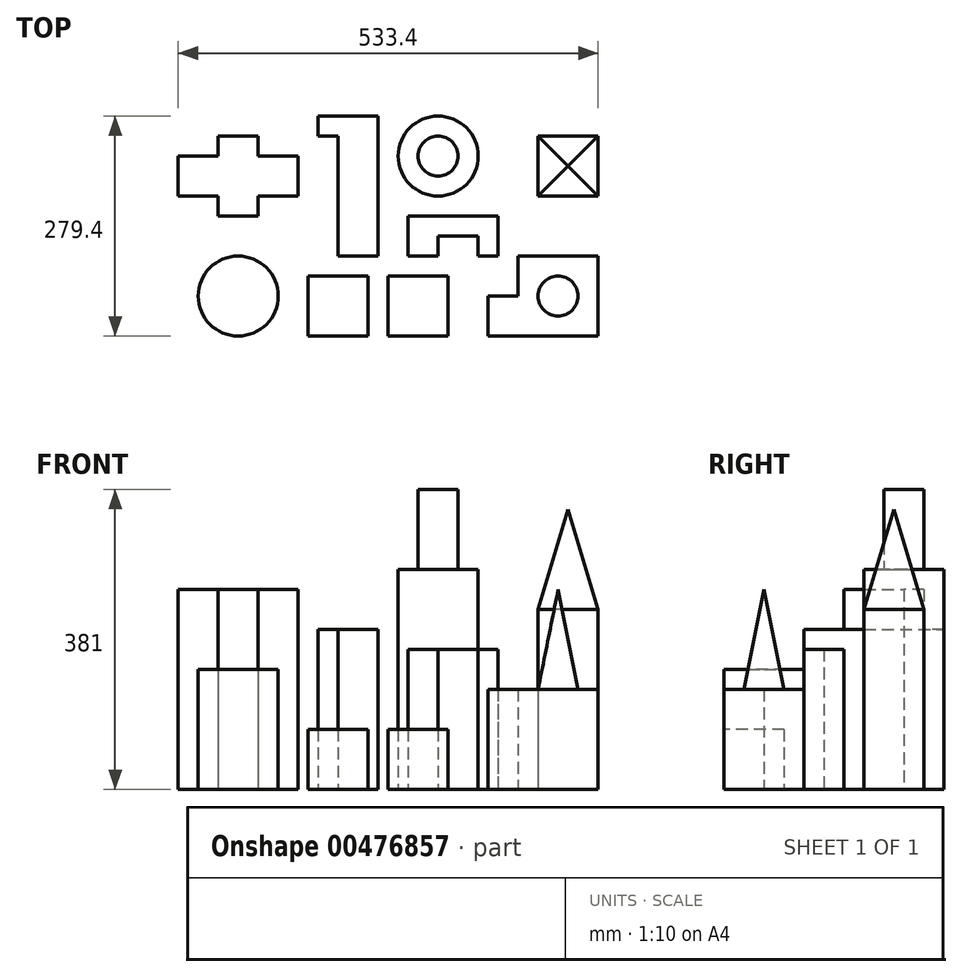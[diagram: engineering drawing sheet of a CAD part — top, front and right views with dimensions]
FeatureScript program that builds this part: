
annotation { "Feature Type Name" : "Feature", "Feature Type Description" : "" }
export const myFeature = defineFeature(function(context is Context, id is Id, definition is map)
    precondition{}
    {
        {
            var Q0;
            Q0=qCreatedBy(makeId("Top.planeOp"),FACE);
            var sketch = newSketch(context, id + "F0", { "sketchPlane" : qUnion([Q0])});
            skLineSegment(sketch, "E0", {"start": v(130.25, 0) * mm, "end": v(130.25, -50.8) * mm});
            skLineSegment(sketch, "E1", {"start": v(130.25, -50.8) * mm, "end": v(269.95, -50.8) * mm});
            skLineSegment(sketch, "E2", {"start": v(269.95, -50.8) * mm, "end": v(269.95, 50.8) * mm});
            skLineSegment(sketch, "E3", {"start": v(269.95, 50.8) * mm, "end": v(168.35, 50.8) * mm});
            skLineSegment(sketch, "E4", {"start": v(168.35, 50.8) * mm, "end": v(168.35, 0) * mm});
            skLineSegment(sketch, "E5", {"start": v(168.35, 0) * mm, "end": v(130.25, 0) * mm});
            skSolve(sketch);
        }
        {
            var Q0;
            Q0 = qSketchRegion(id + "F0", true);
            extrude(context, id + "F1", {"entities" : qUnion([Q0]), "depth" : 127 * mm});
        }
        {
            var Q0;
            Q0=makeQuery(id+"F1.opExtrude","CAP_FACE",FACE,{"disambiguationData":[OSD([sQuery(id+"F0.wireOp",EDGE,"E0"),sQuery(id+"F0.wireOp",EDGE,"E1"),sQuery(id+"F0.wireOp",EDGE,"E2"),sQuery(id+"F0.wireOp",EDGE,"E3"),sQuery(id+"F0.wireOp",EDGE,"E4"),sQuery(id+"F0.wireOp",EDGE,"E5")])],"isStart":false});
            var sketch = newSketch(context, id + "F2", { "sketchPlane" : qUnion([Q0])});
            skCircle(sketch, "E6", {"center": v(219.15, 0) * mm, "radius": 25.4 * mm});
            skSolve(sketch);
        }
        {
            var Q0;
            Q0=makeQuery(id+"F2.imprint","IMPRINT",FACE,{"disambiguationData":[TD([[makeQuery(id+"F2.imprint","IMPRINT",EDGE,{"derivedFrom":sQuery(id+"F2.wireOp",EDGE,"E6")}),1.0]])]});
            extrude(context, id + "F3", {"entities" : qUnion([Q0]), "operationType" : NewBodyOperationType.ADD, "depth" : 127 * mm});
        }
        {
            var Q0;
            Q0=makeQuery(id+"F3.opExtrude","CAP_FACE",FACE,{"disambiguationData":[OSD([sQuery(id+"F2.wireOp",EDGE,"E6")])],"isStart":false});
            chamfer(context, id + "F4", {"entities" : qUnion([Q0]), "chamferType" : ChamferType.TWO_OFFSETS, "width1" : 25.4 * mm, "oppositeDirection" : false, "width2" : 127 * mm, "tangentPropagation" : true});
        }
        {
            var Q0;
            Q0=qCreatedBy(makeId("Top.planeOp"),FACE);
            var sketch = newSketch(context, id + "F5", { "sketchPlane" : qUnion([Q0])});
            skLineSegment(sketch, "E7.bottom", {"start": v(3.25, 25.4) * mm, "end": v(79.45, 25.4) * mm});
            skLineSegment(sketch, "E7.top", {"start": v(3.25, -50.8) * mm, "end": v(79.45, -50.8) * mm});
            skLineSegment(sketch, "E7.left", {"start": v(3.25, 25.4) * mm, "end": v(3.25, -50.8) * mm});
            skLineSegment(sketch, "E7.right", {"start": v(79.45, 25.4) * mm, "end": v(79.45, -50.8) * mm});
            skLineSegment(sketch, "E8.bottom", {"start": v(-98.35, 25.4) * mm, "end": v(-22.15, 25.4) * mm});
            skLineSegment(sketch, "E8.top", {"start": v(-98.35, -50.8) * mm, "end": v(-22.15, -50.8) * mm});
            skLineSegment(sketch, "E8.left", {"start": v(-98.35, 25.4) * mm, "end": v(-98.35, -50.8) * mm});
            skLineSegment(sketch, "E8.right", {"start": v(-22.15, 25.4) * mm, "end": v(-22.15, -50.8) * mm});
            skSolve(sketch);
        }
        {
            var Q0;
            Q0 = qSketchRegion(id + "F5", true);
            extrude(context, id + "F6", {"bodyType" : ToolBodyType.SURFACE, "surfaceEntities" : qUnion([Q0]), "depth" : 76.2 * mm});
        }
        {
            var Q0;
            Q0=qCreatedBy(makeId("Top.planeOp"),FACE);
            var sketch = newSketch(context, id + "F7", { "sketchPlane" : qUnion([Q0])});
            skCircle(sketch, "E9", {"center": v(-187.25, 0) * mm, "radius": 50.8 * mm});
            skSolve(sketch);
        }
        {
            var Q0;
            Q0=makeQuery(id+"F7.imprint","IMPRINT",FACE,{"disambiguationData":[TD([[makeQuery(id+"F7.imprint","IMPRINT",EDGE,{"derivedFrom":sQuery(id+"F7.wireOp",EDGE,"E9")}),1.0]])]});
            var Q1;
            Q1=sQuery(id+"F7.wireOp",EDGE,"E9");
            extrude(context, id + "F8", {"entities" : qUnion([Q0]), "surfaceEntities" : qUnion([Q1]), "depth" : 152.4 * mm});
        }
        {
            var Q0;
            Q0=qCreatedBy(makeId("Top.planeOp"),FACE);
            var sketch = newSketch(context, id + "F9", { "sketchPlane" : qUnion([Q0])});
            skLineSegment(sketch, "E10", {"start": v(-263.45, 177.8) * mm, "end": v(-212.65, 177.8) * mm});
            skLineSegment(sketch, "E11", {"start": v(-212.65, 177.8) * mm, "end": v(-212.65, 203.2) * mm});
            skLineSegment(sketch, "E12", {"start": v(-212.65, 203.2) * mm, "end": v(-161.85, 203.2) * mm});
            skLineSegment(sketch, "E13", {"start": v(-161.85, 203.2) * mm, "end": v(-161.85, 177.8) * mm});
            skLineSegment(sketch, "E14", {"start": v(-161.85, 177.8) * mm, "end": v(-111.05, 177.8) * mm});
            skLineSegment(sketch, "E15", {"start": v(-111.05, 177.8) * mm, "end": v(-111.05, 127) * mm});
            skLineSegment(sketch, "E16", {"start": v(-111.05, 127) * mm, "end": v(-161.85, 127) * mm});
            skLineSegment(sketch, "E17", {"start": v(-161.85, 127) * mm, "end": v(-161.85, 101.6) * mm});
            skLineSegment(sketch, "E18", {"start": v(-161.85, 101.6) * mm, "end": v(-212.65, 101.6) * mm});
            skLineSegment(sketch, "E19", {"start": v(-212.65, 101.6) * mm, "end": v(-212.65, 127) * mm});
            skLineSegment(sketch, "E20", {"start": v(-212.65, 127) * mm, "end": v(-263.45, 127) * mm});
            skLineSegment(sketch, "E21", {"start": v(-263.45, 127) * mm, "end": v(-263.45, 177.8) * mm});
            skSolve(sketch);
        }
        {
            var Q0;
            Q0 = qSketchRegion(id + "F9", true);
            extrude(context, id + "F10", {"entities" : qUnion([Q0]), "depth" : 254 * mm});
        }
        {
            var Q0;
            Q0=qCreatedBy(makeId("Top.planeOp"),FACE);
            var sketch = newSketch(context, id + "F11", { "sketchPlane" : qUnion([Q0])});
            skLineSegment(sketch, "E22", {"start": v(-60.25, 50.8) * mm, "end": v(-9.45, 50.8) * mm});
            skLineSegment(sketch, "E23", {"start": v(-9.45, 50.8) * mm, "end": v(-9.45, 228.6) * mm});
            skLineSegment(sketch, "E24", {"start": v(-9.45, 228.6) * mm, "end": v(-85.65, 228.6) * mm});
            skLineSegment(sketch, "E25", {"start": v(-85.65, 228.6) * mm, "end": v(-85.65, 203.2) * mm});
            skLineSegment(sketch, "E26", {"start": v(-85.65, 203.2) * mm, "end": v(-60.25, 203.2) * mm});
            skLineSegment(sketch, "E27", {"start": v(-60.25, 203.2) * mm, "end": v(-60.25, 50.8) * mm});
            skSolve(sketch);
        }
        {
            var Q0;
            Q0 = qSketchRegion(id + "F11", true);
            extrude(context, id + "F12", {"entities" : qUnion([Q0]), "depth" : 203.2 * mm});
        }
        {
            var Q0;
            Q0=qCreatedBy(makeId("Top.planeOp"),FACE);
            var sketch = newSketch(context, id + "F13", { "sketchPlane" : qUnion([Q0])});
            skCircle(sketch, "E28", {"center": v(66.75, 177.8) * mm, "radius": 50.8 * mm});
            skSolve(sketch);
        }
        {
            var Q0;
            Q0 = qSketchRegion(id + "F13", true);
            extrude(context, id + "F14", {"entities" : qUnion([Q0]), "depth" : 279.4 * mm});
        }
        {
            var Q0;
            Q0=makeQuery(id+"F14.opExtrude","CAP_FACE",FACE,{"disambiguationData":[OSD([sQuery(id+"F13.wireOp",EDGE,"E28")])],"isStart":false});
            var sketch = newSketch(context, id + "F15", { "sketchPlane" : qUnion([Q0])});
            skCircle(sketch, "E29", {"center": v(66.75, 177.8) * mm, "radius": 25.4 * mm});
            skSolve(sketch);
        }
        {
            var Q0;
            Q0=makeQuery(id+"F15.imprint","IMPRINT",FACE,{"disambiguationData":[TD([[makeQuery(id+"F15.imprint","IMPRINT",EDGE,{"derivedFrom":sQuery(id+"F15.wireOp",EDGE,"E29")}),1.0]])]});
            var Q1;
            Q1=sQuery(id+"F15.wireOp",EDGE,"E29");
            extrude(context, id + "F16", {"entities" : qUnion([Q0]), "operationType" : NewBodyOperationType.ADD, "surfaceEntities" : qUnion([Q1]), "depth" : 101.6 * mm});
        }
        {
            var Q0;
            Q0=qCreatedBy(makeId("Top.planeOp"),FACE);
            var sketch = newSketch(context, id + "F17", { "sketchPlane" : qUnion([Q0])});
            skLineSegment(sketch, "E30", {"start": v(28.65, 101.6) * mm, "end": v(28.65, 50.8) * mm});
            skLineSegment(sketch, "E31", {"start": v(28.65, 50.8) * mm, "end": v(66.75, 50.8) * mm});
            skLineSegment(sketch, "E32", {"start": v(66.75, 50.8) * mm, "end": v(66.75, 76.2) * mm});
            skLineSegment(sketch, "E33", {"start": v(66.75, 76.2) * mm, "end": v(117.55, 76.2) * mm});
            skLineSegment(sketch, "E34", {"start": v(117.55, 76.2) * mm, "end": v(117.55, 50.8) * mm});
            skLineSegment(sketch, "E35", {"start": v(117.55, 50.8) * mm, "end": v(142.95, 50.8) * mm});
            skLineSegment(sketch, "E36", {"start": v(142.95, 50.8) * mm, "end": v(142.95, 101.6) * mm});
            skLineSegment(sketch, "E37", {"start": v(142.95, 101.6) * mm, "end": v(28.65, 101.6) * mm});
            skSolve(sketch);
        }
        {
            var Q0;
            Q0 = qSketchRegion(id + "F17", true);
            extrude(context, id + "F18", {"entities" : qUnion([Q0]), "depth" : 177.8 * mm});
        }
        {
            var Q0;
            Q0=qCreatedBy(makeId("Top.planeOp"),FACE);
            var sketch = newSketch(context, id + "F19", { "sketchPlane" : qUnion([Q0])});
            skLineSegment(sketch, "E38.bottom", {"start": v(269.95, 203.2) * mm, "end": v(193.75, 203.2) * mm});
            skLineSegment(sketch, "E38.top", {"start": v(269.95, 127) * mm, "end": v(193.75, 127) * mm});
            skLineSegment(sketch, "E38.left", {"start": v(269.95, 203.2) * mm, "end": v(269.95, 127) * mm});
            skLineSegment(sketch, "E38.right", {"start": v(193.75, 203.2) * mm, "end": v(193.75, 127) * mm});
            skPoint(sketch, "E38.middle", {"position": v(231.85, 165.1) * mm});
            skSolve(sketch);
        }
        {
            var Q0;
            Q0 = qSketchRegion(id + "F19", true);
            extrude(context, id + "F20", {"entities" : qUnion([Q0]), "depth" : 355.6 * mm});
        }
        {
            var Q0;
            Q0=makeQuery(id+"F20.opExtrude","CAP_EDGE",EDGE,{"disambiguationData":[OSD([sQuery(id+"F19.wireOp",EDGE,"E38.top")])],"isStart":false});
            var Q1;
            Q1=makeQuery(id+"F20.opExtrude","CAP_EDGE",EDGE,{"disambiguationData":[OSD([sQuery(id+"F19.wireOp",EDGE,"E38.left")])],"isStart":false});
            var Q2;
            Q2=makeQuery(id+"F20.opExtrude","CAP_EDGE",EDGE,{"disambiguationData":[OSD([sQuery(id+"F19.wireOp",EDGE,"E38.bottom")])],"isStart":false});
            var Q3;
            Q3=makeQuery(id+"F20.opExtrude","CAP_EDGE",EDGE,{"disambiguationData":[OSD([sQuery(id+"F19.wireOp",EDGE,"E38.right")])],"isStart":false});
            chamfer(context, id + "F21", {"entities" : qUnion([Q0, Q1, Q2, Q3]), "chamferType" : ChamferType.TWO_OFFSETS, "width1" : 127 * mm, "oppositeDirection" : false, "width2" : 38.1 * mm, "tangentPropagation" : true});
        }
    });
